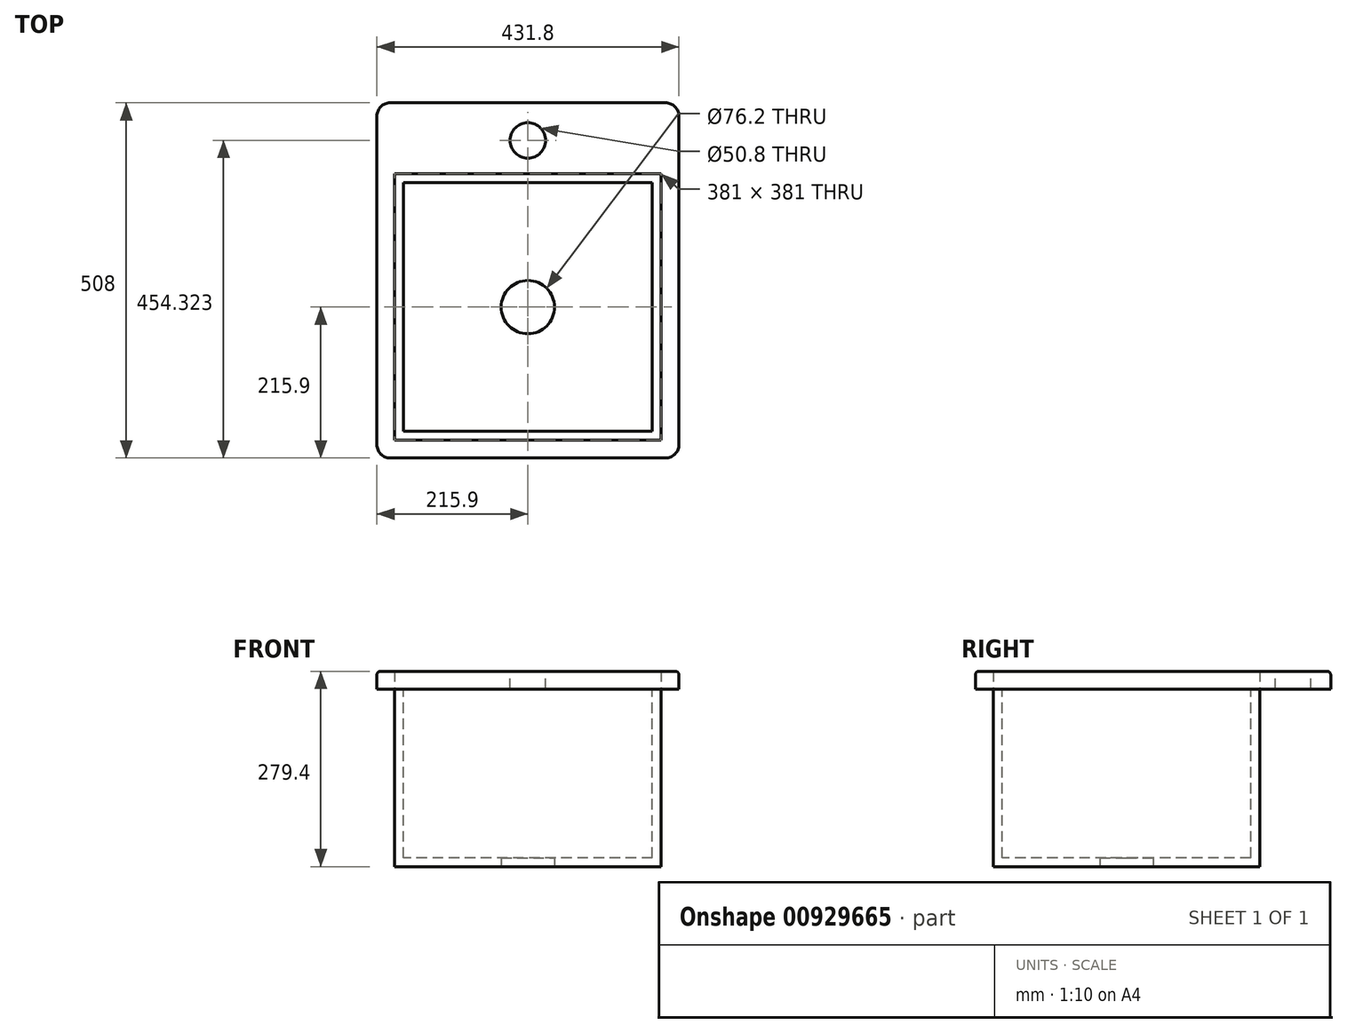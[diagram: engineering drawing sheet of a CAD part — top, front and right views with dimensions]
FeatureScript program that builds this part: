
annotation { "Feature Type Name" : "Feature", "Feature Type Description" : "" }
export const myFeature = defineFeature(function(context is Context, id is Id, definition is map)
    precondition{}
    {
        {
            var Q0;
            Q0=qCreatedBy(makeId("Top.planeOp"),FACE);
            var sketch = newSketch(context, id + "F0", { "sketchPlane" : qUnion([Q0])});
            skCircle(sketch, "E0", {"center": v(0, 0) * mm, "radius": 38.1 * mm});
            skSolve(sketch);
        }
        {
            var Q0;
            Q0=qCreatedBy(makeId("Top.planeOp"),FACE);
            var sketch = newSketch(context, id + "F1", { "sketchPlane" : qUnion([Q0])});
            skLineSegment(sketch, "E1.bottom", {"start": v(190.5, 190.5) * mm, "end": v(-190.5, 190.5) * mm});
            skLineSegment(sketch, "E1.top", {"start": v(190.5, -190.5) * mm, "end": v(-190.5, -190.5) * mm});
            skLineSegment(sketch, "E1.left", {"start": v(190.5, 190.5) * mm, "end": v(190.5, -190.5) * mm});
            skLineSegment(sketch, "E1.right", {"start": v(-190.5, 190.5) * mm, "end": v(-190.5, -190.5) * mm});
            skPoint(sketch, "E1.middle", {"position": v(0, 0) * mm});
            skSolve(sketch);
        }
        {
            var Q0;
            Q0=makeQuery(id+"F1.imprint","IMPRINT",FACE,{"disambiguationData":[TD([[makeQuery(id+"F1.imprint","IMPRINT",EDGE,{"derivedFrom":sQuery(id+"F1.wireOp",EDGE,"E1.bottom")}),1.0]])]});
            var sketch = newSketch(context, id + "F2", { "sketchPlane" : qUnion([Q0])});
            skLineSegment(sketch, "E2", {"start": v(-196.85, 292.1) * mm, "end": v(196.85, 292.1) * mm});
            skLineSegment(sketch, "E3", {"start": v(215.9, 273.05) * mm, "end": v(215.9, -196.85) * mm});
            skLineSegment(sketch, "E4", {"start": v(196.85, -215.9) * mm, "end": v(-196.85, -215.9) * mm});
            skLineSegment(sketch, "E5", {"start": v(-215.9, -196.85) * mm, "end": v(-215.9, 273.05) * mm});
            skPoint(sketch, "E6.visualSharp", {"position": v(-215.9, 292.1) * mm});
            skArc(sketch, "E6.filletArc", {"start": v(-196.85, 292.1) * mm, "mid": v(-210.32, 286.52) * mm, "end": v(-215.9, 273.05) * mm});
            skPoint(sketch, "E7.visualSharp", {"position": v(215.9, 292.1) * mm});
            skArc(sketch, "E7.filletArc", {"start": v(215.9, 273.05) * mm, "mid": v(210.32, 286.52) * mm, "end": v(196.85, 292.1) * mm});
            skPoint(sketch, "E8.visualSharp", {"position": v(215.9, -215.9) * mm});
            skArc(sketch, "E8.filletArc", {"start": v(196.85, -215.9) * mm, "mid": v(210.32, -210.32) * mm, "end": v(215.9, -196.85) * mm});
            skPoint(sketch, "E9.visualSharp", {"position": v(-215.9, -215.9) * mm});
            skArc(sketch, "E9.filletArc", {"start": v(-215.9, -196.85) * mm, "mid": v(-210.32, -210.32) * mm, "end": v(-196.85, -215.9) * mm});
            skSolve(sketch);
        }
        {
            var Q0;
            Q0=makeQuery(id+"F2.imprint","IMPRINT",FACE,{"disambiguationData":[TD([[makeQuery(id+"F2.imprint","IMPRINT",EDGE,{"derivedFrom":sQuery(id+"F2.wireOp",EDGE,"E2")}),-1.0]])]});
            var sketch = newSketch(context, id + "F3", { "sketchPlane" : qUnion([Q0])});
            skCircle(sketch, "E10", {"center": v(0, 238.42) * mm, "radius": 23.45 * mm});
            skSolve(sketch);
        }
        {
            var Q0;
            Q0=makeQuery(id+"F1.imprint","IMPRINT",FACE,{"disambiguationData":[TD([[makeQuery(id+"F1.imprint","IMPRINT",EDGE,{"derivedFrom":sQuery(id+"F1.wireOp",EDGE,"E1.bottom")}),1.0]])]});
            extrude(context, id + "F4", {"entities" : qUnion([Q0]), "oppositeDirection" : true, "depth" : 254 * mm, "offsetDistance" : 25.4 * mm});
        }
        {
            var Q0;
            Q0=makeQuery(id+"F2.imprint","IMPRINT",FACE,{"disambiguationData":[TD([[makeQuery(id+"F2.imprint","IMPRINT",EDGE,{"derivedFrom":sQuery(id+"F2.wireOp",EDGE,"E2")}),-1.0]])]});
            extrude(context, id + "F5", {"entities" : qUnion([Q0]), "operationType" : NewBodyOperationType.ADD, "depth" : 25.4 * mm, "offsetDistance" : 25.4 * mm});
        }
        {
            var Q0;
            Q0=makeQuery(id+"F5.opExtrude","CAP_EDGE",EDGE,{"disambiguationData":[OSD([sQuery(id+"F2.wireOp",EDGE,"E5")])],"isStart":false});
            var Q1;
            Q1=makeQuery(id+"F5.opExtrude","CAP_EDGE",EDGE,{"disambiguationData":[OSD([sQuery(id+"F2.wireOp",EDGE,"E6.filletArc")])],"isStart":false});
            var Q2;
            Q2=makeQuery(id+"F5.opExtrude","CAP_EDGE",EDGE,{"disambiguationData":[OSD([sQuery(id+"F2.wireOp",EDGE,"E2")])],"isStart":false});
            var Q3;
            Q3=makeQuery(id+"F5.opExtrude","CAP_EDGE",EDGE,{"disambiguationData":[OSD([sQuery(id+"F2.wireOp",EDGE,"E7.filletArc")])],"isStart":false});
            var Q4;
            Q4=makeQuery(id+"F5.opExtrude","CAP_EDGE",EDGE,{"disambiguationData":[OSD([sQuery(id+"F2.wireOp",EDGE,"E3")])],"isStart":false});
            var Q5;
            Q5=makeQuery(id+"F5.opExtrude","CAP_EDGE",EDGE,{"disambiguationData":[OSD([sQuery(id+"F2.wireOp",EDGE,"E8.filletArc")])],"isStart":false});
            var Q6;
            Q6=makeQuery(id+"F5.opExtrude","CAP_EDGE",EDGE,{"disambiguationData":[OSD([sQuery(id+"F2.wireOp",EDGE,"E4")])],"isStart":false});
            var Q7;
            Q7=makeQuery(id+"F5.opExtrude","CAP_EDGE",EDGE,{"disambiguationData":[OSD([sQuery(id+"F2.wireOp",EDGE,"E9.filletArc")])],"isStart":false});
            fillet(context, id + "F6", {"entities" : qUnion([Q0, Q1, Q2, Q3, Q4, Q5, Q6, Q7]), "radius" : 5.08 * mm, "tangentPropagation" : true, "allowEdgeOverflow" : false});
        }
        {
            var Q0;
            Q0=sQuery(id+"F3.wireOp",VERTEX,"E10.center");
            var Q1;
            Q1=makeQuery(id+"F5.opExtrude","SWEPT_BODY",BODY,{"disambiguationData":[OSD([sQuery(id+"F1.wireOp",EDGE,"E1.bottom"),sQuery(id+"F1.wireOp",EDGE,"E1.top"),sQuery(id+"F1.wireOp",EDGE,"E1.left"),sQuery(id+"F1.wireOp",EDGE,"E1.right"),sQuery(id+"F2.wireOp",EDGE,"E2"),sQuery(id+"F2.wireOp",EDGE,"E3"),sQuery(id+"F2.wireOp",EDGE,"E4"),sQuery(id+"F2.wireOp",EDGE,"E5"),sQuery(id+"F2.wireOp",EDGE,"E6.filletArc"),sQuery(id+"F2.wireOp",EDGE,"E7.filletArc"),sQuery(id+"F2.wireOp",EDGE,"E8.filletArc"),sQuery(id+"F2.wireOp",EDGE,"E9.filletArc")])]});
            hole(context, id + "F7", {"style" : HoleStyle.SIMPLE, "endStyle" : HoleEndStyle.THROUGH, "oppositeDirection" : true, "holeDiameter" : 50.8 * mm, "majorDiameter" : 6.35 * mm, "isTappedThrough" : true, "tappedDepth" : 12.7 * mm, "tapClearance" : 3, "locations" : qUnion([Q0]), "scope" : qUnion([Q1])});
        }
        {
            var Q0;
            Q0=makeQuery(id+"F4.opExtrude","CAP_FACE",FACE,{"disambiguationData":[OSD([sQuery(id+"F1.wireOp",EDGE,"E1.bottom"),sQuery(id+"F1.wireOp",EDGE,"E1.top"),sQuery(id+"F1.wireOp",EDGE,"E1.left"),sQuery(id+"F1.wireOp",EDGE,"E1.right")])],"isStart":true});
            shell(context, id + "F8", {"entities" : qUnion([Q0]), "thickness" : 12.7 * mm});
        }
        {
            var Q0;
            Q0=sQuery(id+"F0.wireOp",VERTEX,"E0.center");
            var Q1;
            Q1=makeQuery(id+"F4.opExtrude","SWEPT_BODY",BODY,{"disambiguationData":[OSD([sQuery(id+"F1.wireOp",EDGE,"E1.bottom"),sQuery(id+"F1.wireOp",EDGE,"E1.top"),sQuery(id+"F1.wireOp",EDGE,"E1.left"),sQuery(id+"F1.wireOp",EDGE,"E1.right")])]});
            hole(context, id + "F9", {"style" : HoleStyle.SIMPLE, "endStyle" : HoleEndStyle.THROUGH, "holeDiameter" : 76.2 * mm, "majorDiameter" : 6.35 * mm, "isTappedThrough" : true, "tappedDepth" : 12.7 * mm, "tapClearance" : 3, "locations" : qUnion([Q0]), "scope" : qUnion([Q1])});
        }
    });
